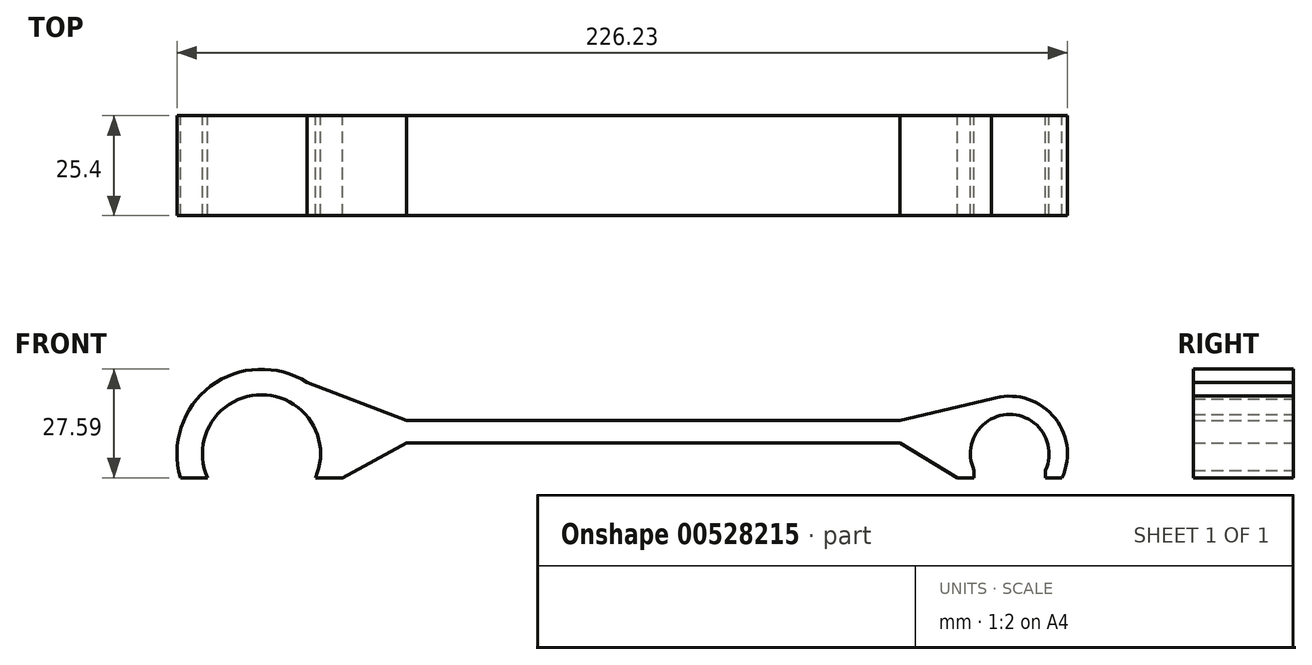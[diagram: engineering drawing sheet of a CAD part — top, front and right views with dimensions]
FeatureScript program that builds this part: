
annotation { "Feature Type Name" : "Feature", "Feature Type Description" : "" }
export const myFeature = defineFeature(function(context is Context, id is Id, definition is map)
    precondition{}
    {
        {
            var Q0;
            Q0=qCreatedBy(makeId("Front.planeOp"),FACE);
            var sketch = newSketch(context, id + "F0", { "sketchPlane" : qUnion([Q0])});
            skArc(sketch, "E0", {"start": v(9.08, -4.19) * mm, "mid": v(0, 10) * mm, "end": v(-9.08, -4.19) * mm});
            skArc(sketch, "E1", {"start": v(13.3, -6.1) * mm, "mid": v(0, 14.64) * mm, "end": v(-13.3, -6.1) * mm});
            skLineSegment(sketch, "E2", {"start": v(-9.08, -4.19) * mm, "end": v(-13.3, -6.1) * mm});
            skLineSegment(sketch, "E3", {"start": v(9.08, -4.19) * mm, "end": v(13.3, -6.1) * mm});
            skLineSegment(sketch, "E4", {"start": v(-9.08, -4.19) * mm, "end": v(9.08, -4.19) * mm, "construction": true});
            skLineSegment(sketch, "E5", {"start": v(-13.3, -6.1) * mm, "end": v(13.3, -6.1) * mm, "construction": true});
            skLineSegment(sketch, "E6", {"start": v(-9.08, -4.19) * mm, "end": v(-9.08, -6.1) * mm});
            skLineSegment(sketch, "E7", {"start": v(-9.08, -6.1) * mm, "end": v(-13.3, -6.1) * mm});
            skLineSegment(sketch, "E8", {"start": v(9.08, -4.19) * mm, "end": v(9.08, -6.1) * mm});
            skLineSegment(sketch, "E9", {"start": v(9.08, -6.1) * mm, "end": v(13.3, -6.1) * mm});
            skLineSegment(sketch, "E10", {"start": v(-10, 0) * mm, "end": v(-175.1, 0) * mm, "construction": true});
            skArc(sketch, "E11", {"start": v(-176.4, -6.1) * mm, "mid": v(-190.1, 15) * mm, "end": v(-203.8, -6.1) * mm});
            skArc(sketch, "E12", {"start": v(-169.5, -6.1) * mm, "mid": v(-190.1, 21.49) * mm, "end": v(-210.7, -6.1) * mm});
            skLineSegment(sketch, "E13", {"start": v(-13.3, -6.1) * mm, "end": v(-210.7, -6.1) * mm, "construction": true});
            skLineSegment(sketch, "E14", {"start": v(-210.7, -6.1) * mm, "end": v(-203.8, -6.1) * mm});
            skLineSegment(sketch, "E15", {"start": v(-176.4, -6.1) * mm, "end": v(-169.5, -6.1) * mm});
            skLineSegment(sketch, "E16", {"start": v(-11.96, 8.43) * mm, "end": v(-170.34, 8.43) * mm});
            skLineSegment(sketch, "E17", {"start": v(-168.79, 2.75) * mm, "end": v(-14.38, 2.75) * mm});
            skLineSegment(sketch, "E18", {"start": v(-27.84, 2.75) * mm, "end": v(-13.3, -6.1) * mm});
            skLineSegment(sketch, "E19", {"start": v(-169.5, -6.1) * mm, "end": v(-153.24, 2.75) * mm});
            skLineSegment(sketch, "E20", {"start": v(-4.65, 13.88) * mm, "end": v(-27.84, 8.43) * mm});
            skLineSegment(sketch, "E21", {"start": v(-178.52, 18.1) * mm, "end": v(-153.24, 8.43) * mm});
            skSolve(sketch);
        }
        {
            var Q0;
            Q0 = qSketchRegion(id + "F0", true);
            extrude(context, id + "F2", {"entities" : qUnion([Q0]), "depth" : 25.4 * mm, "offsetDistance" : 25.4 * mm});
        }
    });
